# Revit family: Mixer-Basin-Caroma Liano
name_source: partatom
category: Plumbing Fixtures
revit_build: Autodesk Revit 2014 (Build: 20131024_2115(x64)
units: mm (PartAtom-declared; Revit-internal decimal feet)

## types (1)
- Standard
    Assembly Code = D2020300
    CW Connection = Yes
    CWFU = 1.19
    Connector Radius = 10 mm  [stored 0.0328084 ft]
    Cost = 0 $
    Default Elevation = 0 mm  [stored 0 ft]
    Description = Proudly Australian designed, the premium Liano mixer range is guaranteed to meet the latest interior design trends. Square inspired outlets and platemount designs offer a distinctive, high quality look. The lever operation means easy and effortless water control while the ceramic disc core eliminates drips and minimises maintenance.
    HW Connection = Yes
    HWFU = 1.19
    Height_ANZRS = 144 mm  [stored 0.472441 ft]
    Length_ANZRS = 46 mm  [stored 0.150919 ft]
    Manufacturer = GWA Bathrooms & Kitchens
    Material_ANZRS = Metal-Chrome-Caroma
    Model = 96142C5A
    ModifiedIssue_ANZRS = 20141212 $
    Type Comments = Caroma Liano Basin Mixer
    URL = http://specify.caroma.com.au
    Vent Connection = No
    WELSRating_ANZRS = WELS 5 Star rated, 6L/min
    Waste Connection = No
    Width_ANZRS = 140 mm  [stored 0.459318 ft]

note: [stored X ft] marks values corroborated as IEEE doubles in the binary element streams (Revit-internal decimal feet)

## geometry (parser evidence)
native form markers: Blend x8, Sweep x1
no freeform markers — native parametric forms only
